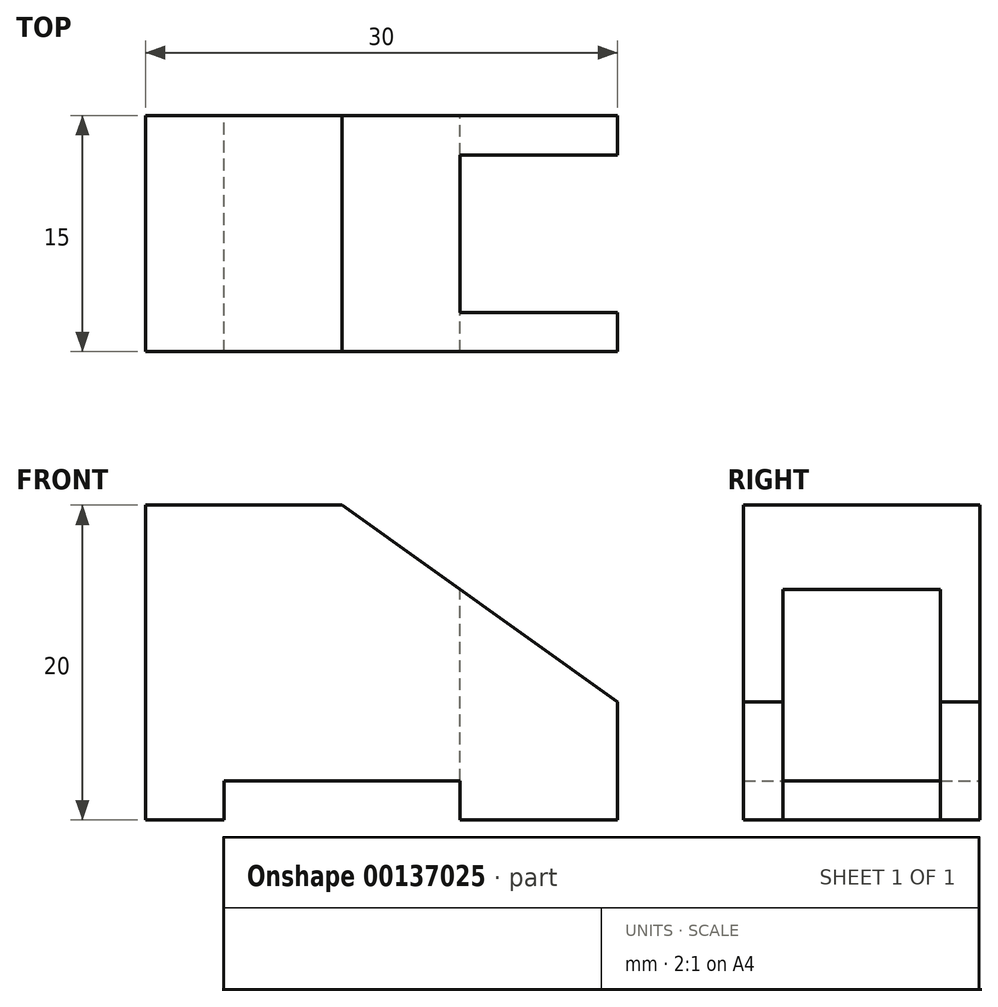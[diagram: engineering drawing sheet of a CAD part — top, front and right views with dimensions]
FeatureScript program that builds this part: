
annotation { "Feature Type Name" : "Feature", "Feature Type Description" : "" }
export const myFeature = defineFeature(function(context is Context, id is Id, definition is map)
    precondition{}
    {
        {
            var Q0;
            Q0=qCreatedBy(makeId("Front.planeOp"),FACE);
            var sketch = newSketch(context, id + "F0", { "sketchPlane" : qUnion([Q0])});
            skLineSegment(sketch, "E0", {"start": v(0, 0) * mm, "end": v(0, 20) * mm});
            skLineSegment(sketch, "E1", {"start": v(0, 20) * mm, "end": v(12.5, 20) * mm});
            skLineSegment(sketch, "E2", {"start": v(12.5, 20) * mm, "end": v(30, 7.5) * mm});
            skLineSegment(sketch, "E3", {"start": v(30, 7.5) * mm, "end": v(30, 0) * mm});
            skLineSegment(sketch, "E4", {"start": v(30, 0) * mm, "end": v(20, 0) * mm});
            skLineSegment(sketch, "E5", {"start": v(20, 0) * mm, "end": v(20, 2.5) * mm});
            skLineSegment(sketch, "E6", {"start": v(20, 2.5) * mm, "end": v(5, 2.5) * mm});
            skLineSegment(sketch, "E7", {"start": v(5, 2.5) * mm, "end": v(5, 0) * mm});
            skLineSegment(sketch, "E8", {"start": v(5, 0) * mm, "end": v(0, 0) * mm});
            skSolve(sketch);
        }
        {
            var Q0;
            Q0 = qSketchRegion(id + "F0", true);
            extrude(context, id + "F1", {"entities" : qUnion([Q0]), "endBound" : BoundingType.SYMMETRIC, "depth" : 15 * mm});
        }
        {
            var Q0;
            Q0=makeQuery(id+"F1.opExtrude","SWEPT_FACE",FACE,{"disambiguationData":[OSD([sQuery(id+"F0.wireOp",EDGE,"E1")])]});
            var sketch = newSketch(context, id + "F2", { "sketchPlane" : qUnion([Q0])});
            skLineSegment(sketch, "E9", {"start": v(20, 5) * mm, "end": v(20, -5) * mm});
            skLineSegment(sketch, "E10", {"start": v(20, -5) * mm, "end": v(30, -5) * mm});
            skLineSegment(sketch, "E11", {"start": v(30, -5) * mm, "end": v(30, 5) * mm});
            skLineSegment(sketch, "E12", {"start": v(30, 5) * mm, "end": v(20, 5) * mm});
            skSolve(sketch);
        }
        {
            var Q0;
            Q0=makeQuery(id+"F2.imprint","IMPRINT",FACE,{"disambiguationData":[TD([[makeQuery(id+"F2.imprint","IMPRINT",EDGE,{"derivedFrom":sQuery(id+"F2.wireOp",EDGE,"E9")}),1.0]])]});
            extrude(context, id + "F3", {"entities" : qUnion([Q0]), "operationType" : NewBodyOperationType.REMOVE, "endBound" : BoundingType.THROUGH_ALL, "oppositeDirection" : true, "depth" : 25 * mm});
        }
    });
